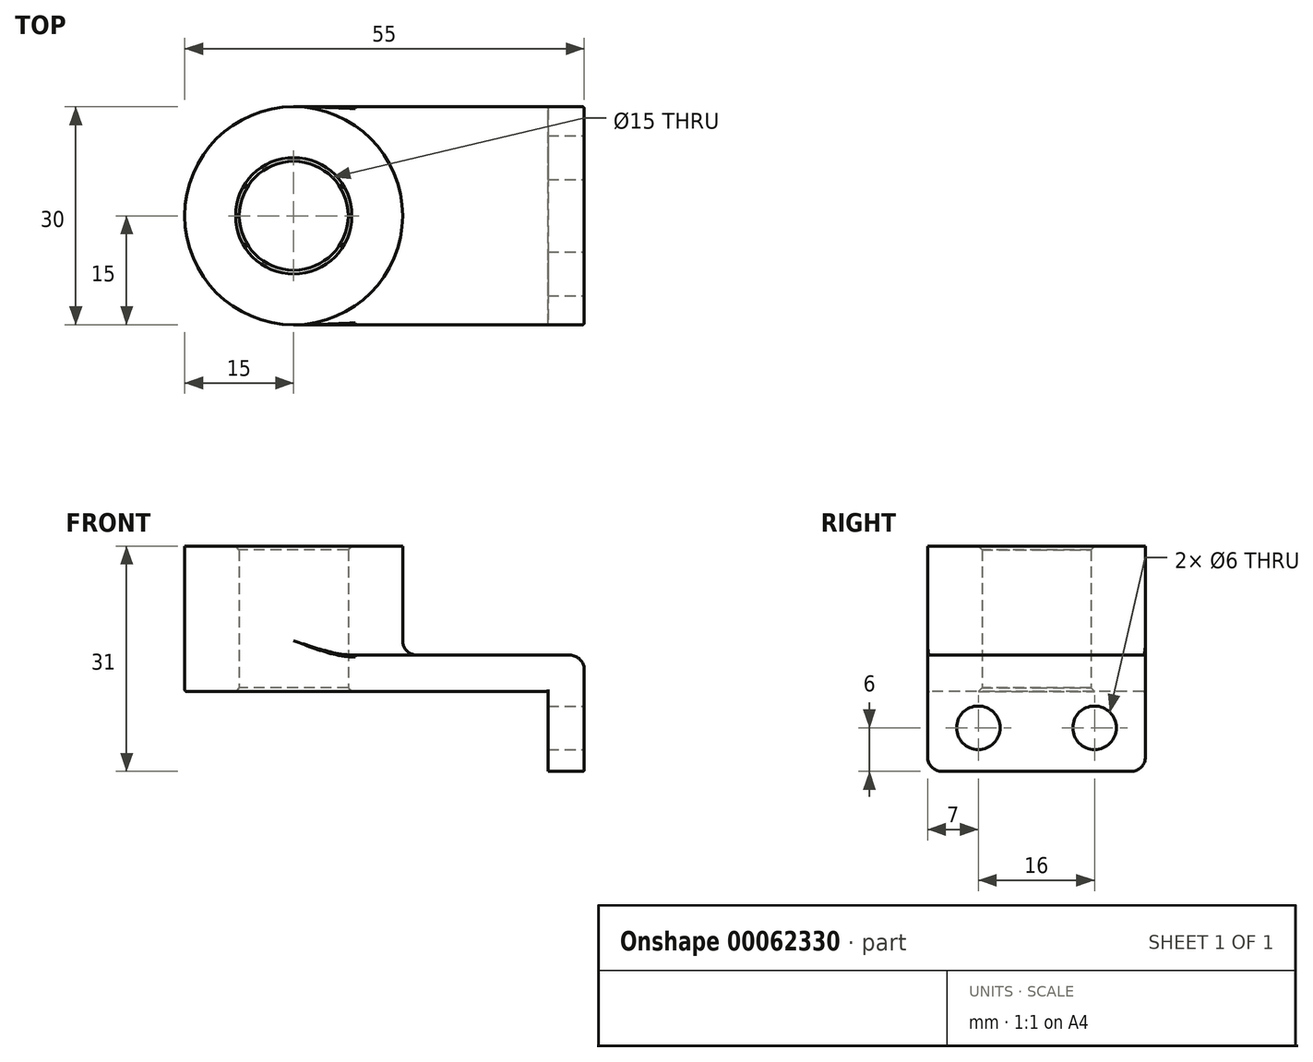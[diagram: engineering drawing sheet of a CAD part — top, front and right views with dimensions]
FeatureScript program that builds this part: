
annotation { "Feature Type Name" : "Feature", "Feature Type Description" : "" }
export const myFeature = defineFeature(function(context is Context, id is Id, definition is map)
    precondition{}
    {
        {
            var Q0;
            Q0=qCreatedBy(makeId("Top.planeOp"),FACE);
            var sketch = newSketch(context, id + "F0", { "sketchPlane" : qUnion([Q0])});
            skLineSegment(sketch, "E0.rect.bottom", {"start": v(20, 15) * mm, "end": v(-20, 15) * mm});
            skLineSegment(sketch, "E0.rect.top", {"start": v(20, -15) * mm, "end": v(-20, -15) * mm});
            skLineSegment(sketch, "E0.rect.left", {"start": v(20, 15) * mm, "end": v(20, -15) * mm});
            skLineSegment(sketch, "E0.rect.right", {"start": v(-20, 15) * mm, "end": v(-20, -15) * mm});
            skPoint(sketch, "E0.rect.middle", {"position": v(0, 0) * mm});
            skCircle(sketch, "E1", {"center": v(-20, 0) * mm, "radius": 15 * mm});
            skCircle(sketch, "E2", {"center": v(-20, 0) * mm, "radius": 7.5 * mm});
            skSolve(sketch);
        }
        {
            var Q0;
            Q0 = qSketchRegion(id + "F0", true);
            extrude(context, id + "F1", {"entities" : qUnion([Q0]), "depth" : 5 * mm});
        }
        {
            var Q0;
            {var subQ1=sQuery(id+"F0.wireOp",EDGE,"E0.rect.right");var subQ3=sQuery(id+"F0.wireOp",EDGE,"E2");var subQ4=makeQuery(id+"F0.imprint","INTERSECT",VERTEX,{"disambiguationData":[OD(0.0)],"derivedFrom":[subQ1,subQ3]});Q0=makeQuery(id+"F0.imprint","IMPRINT",FACE,{"disambiguationData":[TD([[makeQuery(id+"F0.imprint","IMPRINT",EDGE,{"disambiguationData":[TD([[subQ4,-1.0]])],"derivedFrom":subQ3}),-1.0]])]});}
            var Q1;
            {var subQ1=sQuery(id+"F0.wireOp",EDGE,"E0.rect.right");var subQ3=sQuery(id+"F0.wireOp",EDGE,"E2");var subQ4=makeQuery(id+"F0.imprint","INTERSECT",VERTEX,{"disambiguationData":[OD(0.0)],"derivedFrom":[subQ1,subQ3]});Q1=makeQuery(id+"F0.imprint","IMPRINT",FACE,{"disambiguationData":[TD([[makeQuery(id+"F0.imprint","IMPRINT",EDGE,{"disambiguationData":[TD([[subQ4,1.0]])],"derivedFrom":subQ3}),-1.0]])]});}
            extrude(context, id + "F2", {"entities" : qUnion([Q0, Q1]), "operationType" : NewBodyOperationType.ADD, "depth" : 20 * mm});
        }
        {
            var Q0;
            Q0=makeQuery(id+"F1.opExtrude","SWEPT_FACE",FACE,{"disambiguationData":[OSD([sQuery(id+"F0.wireOp",EDGE,"E0.rect.left")])]});
            var sketch = newSketch(context, id + "F3", { "sketchPlane" : qUnion([Q0])});
            skLineSegment(sketch, "E3.bottom", {"start": v(-15, 5) * mm, "end": v(15, 5) * mm});
            skLineSegment(sketch, "E3.top", {"start": v(-15, -11) * mm, "end": v(15, -11) * mm});
            skLineSegment(sketch, "E3.left", {"start": v(-15, 5) * mm, "end": v(-15, -11) * mm});
            skLineSegment(sketch, "E3.right", {"start": v(15, 5) * mm, "end": v(15, -11) * mm});
            skLineSegment(sketch, "E4", {"start": v(0, -0.45) * mm, "end": v(0, -11) * mm, "construction": true});
            skCircle(sketch, "E5", {"center": v(-8, -5) * mm, "radius": 3 * mm});
            skCircle(sketch, "E6.MirrorC", {"center": v(8, -5) * mm, "radius": 3 * mm});
            skSolve(sketch);
        }
        {
            var Q0;
            {var subQ2=sQuery(id+"F3.wireOp",EDGE,"E3.top");Q0=makeQuery(id+"F3.imprint","IMPRINT",FACE,{"disambiguationData":[TD([[makeQuery(id+"F3.imprint","IMPRINT",EDGE,{"derivedFrom":subQ2}),1.0]])]});}
            extrude(context, id + "F4", {"entities" : qUnion([Q0]), "operationType" : NewBodyOperationType.ADD, "oppositeDirection" : true, "depth" : 5 * mm});
        }
        {
            var Q0;
            {var subQ0=sQuery(id+"F0.wireOp",EDGE,"E1");Q0=makeQuery(id+"F2.boolean.opBoolean","INTERSECT",EDGE,{"derivedFrom":[makeQuery(id+"F1.opExtrude","CAP_FACE",FACE,{"disambiguationData":[OSD([sQuery(id+"F0.wireOp",EDGE,"E0.rect.bottom"),sQuery(id+"F0.wireOp",EDGE,"E0.rect.top"),sQuery(id+"F0.wireOp",EDGE,"E0.rect.left"),subQ0,sQuery(id+"F0.wireOp",EDGE,"E2")])],"isStart":false}),makeQuery(id+"F2.opExtrude","SWEPT_FACE",FACE,{"disambiguationData":[OSD([subQ0])]})]});}
            var Q1;
            Q1=makeQuery(id+"F1.opExtrude","CAP_EDGE",EDGE,{"disambiguationData":[OSD([sQuery(id+"F0.wireOp",EDGE,"E0.rect.left")])],"isStart":false});
            var Q2;
            Q2=makeQuery(id+"F4.opExtrude","SWEPT_EDGE",EDGE,{"disambiguationData":[OSD([sQuery(id+"F3.wireOp",EDGE,"E3.top"),sQuery(id+"F3.wireOp",EDGE,"E3.left")])]});
            var Q3;
            Q3=makeQuery(id+"F4.opExtrude","SWEPT_EDGE",EDGE,{"disambiguationData":[OSD([sQuery(id+"F3.wireOp",EDGE,"E3.top"),sQuery(id+"F3.wireOp",EDGE,"E3.right")])]});
            fillet(context, id + "F5", {"entities" : qUnion([Q0, Q1, Q2, Q3]), "radius" : 2 * mm, "tangentPropagation" : true, "allowEdgeOverflow" : false});
        }
        {
            var Q0;
            Q0=makeQuery(id+"F1.opExtrude","CAP_EDGE",EDGE,{"disambiguationData":[OSD([sQuery(id+"F0.wireOp",EDGE,"E0.rect.top")])],"isStart":false});
            var Q1;
            Q1=makeQuery(id+"F1.opExtrude","CAP_EDGE",EDGE,{"disambiguationData":[OSD([sQuery(id+"F0.wireOp",EDGE,"E0.rect.top")])],"isStart":true});
            var Q2;
            Q2=makeQuery(id+"F4.opExtrude","CAP_EDGE",EDGE,{"disambiguationData":[OSD([sQuery(id+"F0.wireOp",EDGE,"E0.rect.left")])],"isStart":false});
            fillet(context, id + "F6", {"entities" : qUnion([Q0, Q1, Q2]), "radius" : (1 / 4) * mm, "tangentPropagation" : true, "allowEdgeOverflow" : false});
        }
        {
            var Q0;
            {var subQ0=sQuery(id+"F0.wireOp",EDGE,"E2");Q0=makeQuery(id+"F2.boolean.opBoolean","MERGE",FACE,{"derivedFrom":[makeQuery(id+"F1.opExtrude","SWEPT_FACE",FACE,{"disambiguationData":[OSD([subQ0])]}),makeQuery(id+"F2.opExtrude","SWEPT_FACE",FACE,{"disambiguationData":[OSD([subQ0])]})]});}
            chamfer(context, id + "F7", {"entities" : qUnion([Q0]), "width" : (1 / 2) * mm, "tangentPropagation" : true});
        }
    });
